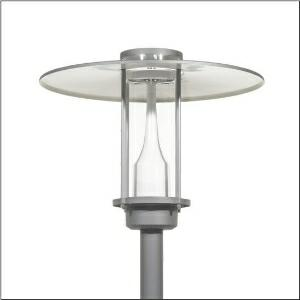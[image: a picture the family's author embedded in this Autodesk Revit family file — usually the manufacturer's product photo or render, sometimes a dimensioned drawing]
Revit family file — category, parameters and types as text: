
# Revit family: city-light_plus_iq___st1_2a_5xa5275ef14h000022_292e
name_source: partatom
category: Lighting Fixtures
units: mm (PartAtom-declared; Revit-internal decimal feet)

## family parameters
Cut with Voids When Loaded = No
Host = Face
Light Source = No
Part Type = Normal
Room Calculation Point = No
Round Connector Dimension = Use Diameter
Shared = No

## types (1)
- --- (1 x LED, 1470 lm, 10.5 W, 3000K)
    Apparent Load = 11 VA
    CIE Flux Codes = 22 62 93 97 100
    Color Rendering = 70
    Color Temperature = 3000K
    Default Elevation = 1800 mm
    Description = City-Light Plus iQ, mast luminaire, Module 540 iQ-SR, primary light control with 3 zone facetted reflector, of plastic, silver coated, highly specular, structured, primary optical cover: cover, of PMMA, transparent, light distribution: ST1.2a, light emission: direct distribution, primary light characteristic: asymmetric, installation type: post-top, LED, High Power LED, rated luminous flux: 1.470lm, luminous efficacy: 140lm/W, light colour: 730, colour temperature: 3000K, control gear: iQ Street-Remote, control: Street-Remote, Auto-Match, Temp-Guard, Lumen-Switch, Night-Set, Smart-Wire, Light-Fading, Desk-Remote (wireless, voltage-free reading and setting of iQ features in the workshop via application-optimized NFC function/RFID function), optimised constant luminous flux control (CLO 2.0), pre-setting: logarithmic dimming characteristic, mains connection: 230..240V, AC, 50/60Hz, connection cable pre-assembled, cable length: 5,5m, wiring characteristics: H07RN-F, start of lifetime: 11W, end of service life: 11W, reduction: 5W, luminaire housing, upper part, of glass-fibre reinforced polyester, coated, SITECO metallic grey (DB 702S), diameter: 750mm, height: 590mm, spigot size: d x l = 76 x 70mm (post-top) | with reducer (optional accessory) 60 x 70mm, mounting height: 3..5m, post-top mast mounting element, of diecast aluminium, coated, SITECO metallic grey (DB 702S), Module 540 iQ-SR, traffic white (RAL 9016), equipment: standard, protection rating (complete): IP65, insulation class (complete): insulation class II (safety insulation), certification: CE, ENEC, VDE, packaging unit: 1 piece

Light Distribution: ST1.2a
    Height = 590 mm
    Lamp = 1 x LED
    Lamp Light Flux = 1470 lm
    Lamp Power = 10.5 W
    Lamp count = 1
    Length = 750 mm
    Luminous efficacy = 140 lm/W
    Manufacturer = Siteco
    ModVariant = No
    Model = 5XA5275EF14H000022
    Number of Poles = 1
    OnlyDefault = Yes
    Power Factor = 1
    Product Name = City-Light Plus iQ | ST1.2a
    Product group = mast luminaire | pylon top
    ProductGroupID = 6100
    Protection Class = Protection class II
    Protection Degree = IP 65
    RLX_Detail_Level = 1
    RLX_Emergency_Light_Flux = 0 lm
    RLX_Emergency_Type = 0
    RLX_Emergency_Type_DB = No
    RlxData = <blob elided: 51441 chars, md5=5eb64c0e>
    Socket = socket
    Standby Power = 0 W
    System Light Flux = 1470 lm
    System Power = 11 W
    Type Comments = factory setting: luminous flux: 100 % | dim-lin: 254 | 419 mA
    Type Image = l_1006456.jpg
    URL = http://relux.com
    VarID = @adj_159529
    Voltage = 0 V
    Weight = 0.00 kg
    Width = 0 mm  [stored 0 ft]

note: [stored X ft] marks values corroborated as IEEE doubles in the binary element streams (Revit-internal decimal feet)

## geometry (parser evidence)
native form markers: Blend x4, Sweep x11
no freeform markers — native parametric forms only
